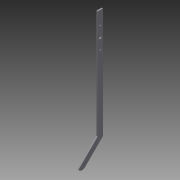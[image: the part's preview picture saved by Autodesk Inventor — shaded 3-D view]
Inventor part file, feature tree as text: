
AUTODESK INVENTOR PART (.ipt)
format: ipt  version: 2013 (Build 170138000, 138)  size: 165,376 bytes
history: native  units: in
note: dims shown in document units (in); Inventor stores cm internally (conversion verified against a paired STEP export)
features: extrude x9, sketch x8
ambient origin geometry x8: Origin, YZ Plane, XZ Plane, XY Plane, X Axis, Y Axis, Z Axis, Center Point
bodies: Solid1 (feature_tree)
feature tree (17):
  extrude  "Extrusion1"  Depth=0.5in
  extrude  "Extrusion2"  Depth=0.5in
  extrude  "Extrusion3"  Depth=16.484in
  extrude  "Extrusion4"  Depth=5.14in
  extrude  "Extrusion5"  Depth=1.0in
  extrude  "Extrusion8"  Depth=6.0in
  extrude  "Extrusion9"  Depth=1.0in
  extrude  "Extrusion11"  Depth=1.0in TaperAngle=0.0deg
  extrude  "Extrusion12"  Depth=0.25in
  sketch  "Sketch1"  dims[d0=0.25in d1=0.5in]
  sketch  "Sketch2"  dims[d2=0.0in d3=0.5in]
  sketch  "Sketch3"  dims[d4=90.0deg d5=16.484in]
  sketch  "Sketch4"  dims[d6=1.0in d7=5.14in]
  sketch  "Sketch5"  dims[d8=135.0deg d9=1.0in]
  sketch  "Sketch8"  dims[d10=90.0deg d11=6.0in]
  sketch  "Sketch9"  dims[d12=90.0deg d13=1.0in]
  sketch  "Sketch11"  dims[d14=180.0deg d15=1.0in d16=0.0in d17=0.25in d18=0.75in d19=1.0in d20=0.0in d21=5.0in d22=0.0in d23=0.75in d24=0.0in d25=1.0in d26=5.0in d27=5.0in d28=0.0in d43=4.0in d44=0.0in d45=0.5in d46=1.0in d47=0.0in d52=0.25in d53=0.0in d54=2.5in d55=90.0deg d56=4.0in d57=90.0deg d58=0.25in d59=0.25in d60=0.25in d61=0.0in]
